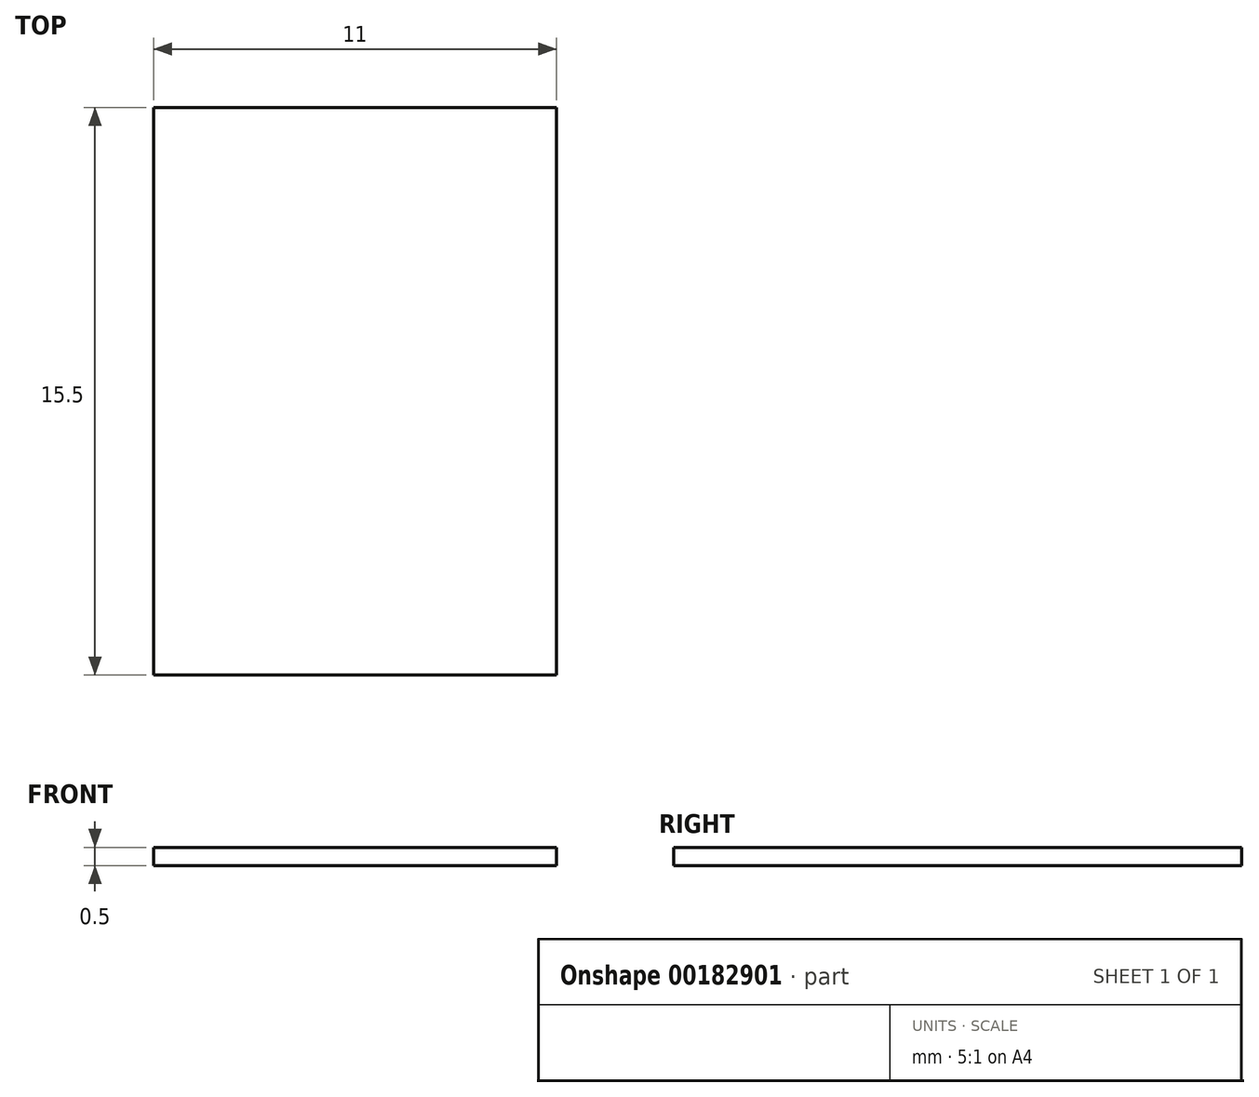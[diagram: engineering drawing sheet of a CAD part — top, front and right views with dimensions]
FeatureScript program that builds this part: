
annotation { "Feature Type Name" : "Feature", "Feature Type Description" : "" }
export const myFeature = defineFeature(function(context is Context, id is Id, definition is map)
    precondition{}
    {
        {
            var Q0;
            Q0=qCreatedBy(makeId("Top.planeOp"),FACE);
            var sketch = newSketch(context, id + "F0", { "sketchPlane" : qUnion([Q0])});
            skLineSegment(sketch, "E0.bottom", {"start": v(-9.7, 10.66) * mm, "end": v(1.3, 10.66) * mm});
            skLineSegment(sketch, "E0.top", {"start": v(-9.7, -4.84) * mm, "end": v(1.3, -4.84) * mm});
            skLineSegment(sketch, "E0.left", {"start": v(-9.7, 10.66) * mm, "end": v(-9.7, -4.84) * mm});
            skLineSegment(sketch, "E0.right", {"start": v(1.3, 10.66) * mm, "end": v(1.3, -4.84) * mm});
            skSolve(sketch);
        }
        {
            var Q0;
            Q0=makeQuery(id+"F0.imprint","IMPRINT",FACE,{"disambiguationData":[TD([[makeQuery(id+"F0.imprint","IMPRINT",EDGE,{"derivedFrom":sQuery(id+"F0.wireOp",EDGE,"E0.bottom")}),-1.0]])]});
            extrude(context, id + "F1", {"entities" : qUnion([Q0]), "depth" : 0.5 * mm});
        }
    });
